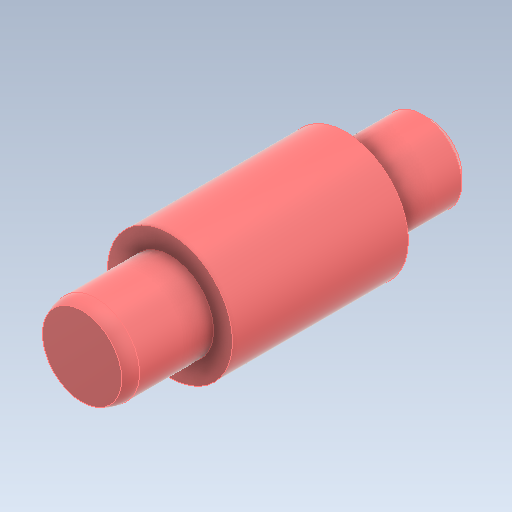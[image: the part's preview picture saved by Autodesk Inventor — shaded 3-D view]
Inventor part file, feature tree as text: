
AUTODESK INVENTOR PART (.ipt)
format: ipt  version: 2021 (Build 250183000, 183)  size: 153,600 bytes
history: native  units: in
note: dims shown in document units (in); Inventor stores cm internally (conversion verified against a paired STEP export)
features: revolve x1, fillet x1, sketch x1
ambient origin geometry x8: Origin, YZ Plane, XZ Plane, XY Plane, X Axis, Y Axis, Z Axis, Center Point
bodies: Solid1 (feature_tree)
feature tree (3):
  revolve  "Revolution1"  [1 undecoded]
  fillet  "Fillet1"  Radius=1.7717in
  sketch  "Sketch1"  dims[d15=90.0deg d19=0.2756in d26=1.7717in d27=0.8465in d28=0.8465in d29=0.0787in d30=0.0787in]
note: 1 required parameter value undecoded (feature->parameter linkage not recoverable at this tier; creation-order binding heuristic only, values carry confidence <= 0.55)
